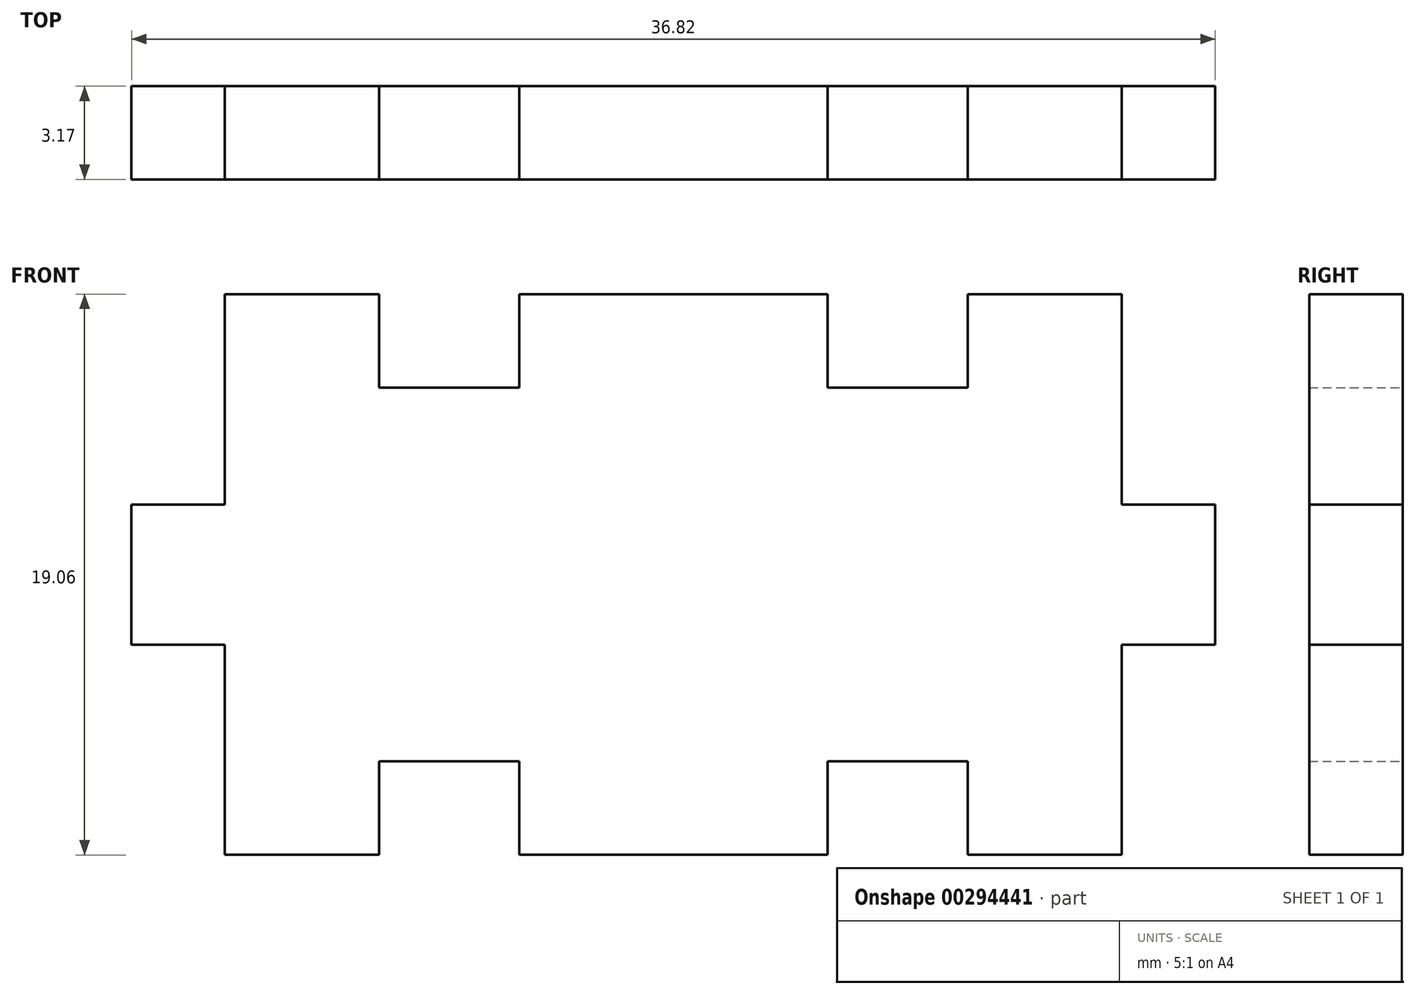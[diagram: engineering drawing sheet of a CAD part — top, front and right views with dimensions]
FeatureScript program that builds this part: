
annotation { "Feature Type Name" : "Feature", "Feature Type Description" : "" }
export const myFeature = defineFeature(function(context is Context, id is Id, definition is map)
    precondition{}
    {
        {
            var Q0;
            Q0=qCreatedBy(makeId("Front.planeOp"),FACE);
            var sketch = newSketch(context, id + "F0", { "sketchPlane" : qUnion([Q0])});
            skLineSegment(sketch, "E0.bottom", {"start": v(15.24, 9.52) * mm, "end": v(-15.24, 9.53) * mm});
            skLineSegment(sketch, "E0.top", {"start": v(15.24, -9.53) * mm, "end": v(-15.24, -9.52) * mm});
            skLineSegment(sketch, "E0.left", {"start": v(15.24, 9.53) * mm, "end": v(15.24, -9.53) * mm});
            skLineSegment(sketch, "E0.right", {"start": v(-15.24, 9.53) * mm, "end": v(-15.24, -9.53) * mm});
            skPoint(sketch, "E0.middle", {"position": v(0, 0) * mm});
            skLineSegment(sketch, "E1", {"start": v(0, 9.53) * mm, "end": v(0, -9.53) * mm});
            skLineSegment(sketch, "E2", {"start": v(-15.24, 0) * mm, "end": v(15.24, 0) * mm});
            skLineSegment(sketch, "E3", {"start": v(7.62, 9.53) * mm, "end": v(7.62, -9.53) * mm});
            skLineSegment(sketch, "E4", {"start": v(-7.62, 9.53) * mm, "end": v(-7.62, -9.53) * mm});
            skLineSegment(sketch, "E5.bottom", {"start": v(18.41, 2.38) * mm, "end": v(12.06, 2.38) * mm});
            skLineSegment(sketch, "E5.top", {"start": v(18.41, -2.38) * mm, "end": v(12.06, -2.38) * mm});
            skLineSegment(sketch, "E5.left", {"start": v(18.41, 2.38) * mm, "end": v(18.41, -2.38) * mm});
            skLineSegment(sketch, "E5.right", {"start": v(12.07, 2.38) * mm, "end": v(12.07, -2.38) * mm});
            skPoint(sketch, "E5.middle", {"position": v(15.24, 0) * mm});
            skLineSegment(sketch, "E6.bottom", {"start": v(-18.41, 2.38) * mm, "end": v(-12.07, 2.38) * mm});
            skLineSegment(sketch, "E6.top", {"start": v(-18.41, -2.38) * mm, "end": v(-12.07, -2.38) * mm});
            skLineSegment(sketch, "E6.left", {"start": v(-18.41, 2.38) * mm, "end": v(-18.41, -2.38) * mm});
            skLineSegment(sketch, "E6.right", {"start": v(-12.07, 2.38) * mm, "end": v(-12.07, -2.38) * mm});
            skPoint(sketch, "E6.middle", {"position": v(-15.24, 0) * mm});
            skLineSegment(sketch, "E7.bottom", {"start": v(10, 6.35) * mm, "end": v(5.24, 6.35) * mm});
            skLineSegment(sketch, "E7.top", {"start": v(10, 12.7) * mm, "end": v(5.24, 12.7) * mm});
            skLineSegment(sketch, "E7.left", {"start": v(10, 6.35) * mm, "end": v(10, 12.7) * mm});
            skLineSegment(sketch, "E7.right", {"start": v(5.24, 6.35) * mm, "end": v(5.24, 12.7) * mm});
            skPoint(sketch, "E7.middle", {"position": v(7.62, 9.53) * mm});
            skLineSegment(sketch, "E8.bottom", {"start": v(-5.24, 6.35) * mm, "end": v(-10, 6.35) * mm});
            skLineSegment(sketch, "E8.top", {"start": v(-5.24, 12.7) * mm, "end": v(-10, 12.7) * mm});
            skLineSegment(sketch, "E8.left", {"start": v(-5.24, 6.35) * mm, "end": v(-5.24, 12.7) * mm});
            skLineSegment(sketch, "E8.right", {"start": v(-10, 6.35) * mm, "end": v(-10, 12.7) * mm});
            skPoint(sketch, "E8.middle", {"position": v(-7.62, 9.53) * mm});
            skLineSegment(sketch, "E9.bottom", {"start": v(-5.24, -6.35) * mm, "end": v(-10, -6.35) * mm});
            skLineSegment(sketch, "E9.top", {"start": v(-5.24, -12.7) * mm, "end": v(-10, -12.7) * mm});
            skLineSegment(sketch, "E9.left", {"start": v(-5.24, -6.35) * mm, "end": v(-5.24, -12.7) * mm});
            skLineSegment(sketch, "E9.right", {"start": v(-10, -6.35) * mm, "end": v(-10, -12.7) * mm});
            skPoint(sketch, "E9.middle", {"position": v(-7.62, -9.53) * mm});
            skLineSegment(sketch, "E10.bottom", {"start": v(10, -6.35) * mm, "end": v(5.24, -6.35) * mm});
            skLineSegment(sketch, "E10.top", {"start": v(10, -12.7) * mm, "end": v(5.24, -12.7) * mm});
            skLineSegment(sketch, "E10.left", {"start": v(10, -6.35) * mm, "end": v(10, -12.7) * mm});
            skLineSegment(sketch, "E10.right", {"start": v(5.24, -6.35) * mm, "end": v(5.24, -12.7) * mm});
            skPoint(sketch, "E10.middle", {"position": v(7.62, -9.53) * mm});
            skSolve(sketch);
        }
        {
            var Q0;
            {var subQ0=sQuery(id+"F0.wireOp",EDGE,"E0.right");var subQ1=sQuery(id+"F0.wireOp",EDGE,"E0.bottom");var subQ2=makeQuery(id+"F0.imprint","INTERSECT",VERTEX,{"derivedFrom":[subQ1,subQ0]});Q0=makeQuery(id+"F0.imprint","IMPRINT",FACE,{"disambiguationData":[TD([[makeQuery(id+"F0.imprint","IMPRINT",EDGE,{"disambiguationData":[TD([[subQ2,1.0]])],"derivedFrom":subQ1}),1.0]])]});}
            var Q1;
            {var subQ5=sQuery(id+"F0.wireOp",EDGE,"E1");var subQ6=sQuery(id+"F0.wireOp",EDGE,"E0.bottom");var subQ7=makeQuery(id+"F0.imprint","INTERSECT",VERTEX,{"derivedFrom":[subQ6,subQ5]});Q1=makeQuery(id+"F0.imprint","IMPRINT",FACE,{"disambiguationData":[TD([[makeQuery(id+"F0.imprint","IMPRINT",EDGE,{"disambiguationData":[TD([[subQ7,-1.0]])],"derivedFrom":subQ6}),1.0]])]});}
            var Q2;
            {var subQ1=sQuery(id+"F0.wireOp",EDGE,"E1");var subQ5=sQuery(id+"F0.wireOp",EDGE,"E0.bottom");var subQ6=makeQuery(id+"F0.imprint","INTERSECT",VERTEX,{"derivedFrom":[subQ5,subQ1]});Q2=makeQuery(id+"F0.imprint","IMPRINT",FACE,{"disambiguationData":[TD([[makeQuery(id+"F0.imprint","IMPRINT",EDGE,{"disambiguationData":[TD([[subQ6,1.0]])],"derivedFrom":subQ5}),1.0]])]});}
            var Q3;
            {var subQ5=sQuery(id+"F0.wireOp",EDGE,"E0.left");var subQ6=sQuery(id+"F0.wireOp",EDGE,"E0.bottom");var subQ7=makeQuery(id+"F0.imprint","INTERSECT",VERTEX,{"derivedFrom":[subQ6,subQ5]});Q3=makeQuery(id+"F0.imprint","IMPRINT",FACE,{"disambiguationData":[TD([[makeQuery(id+"F0.imprint","IMPRINT",EDGE,{"disambiguationData":[TD([[subQ7,-1.0]])],"derivedFrom":subQ6}),1.0]])]});}
            var Q4;
            {var subQ0=sQuery(id+"F0.wireOp",EDGE,"E2");var subQ1=sQuery(id+"F0.wireOp",EDGE,"E0.left");var subQ2=makeQuery(id+"F0.imprint","INTERSECT",VERTEX,{"derivedFrom":[subQ1,subQ0]});Q4=makeQuery(id+"F0.imprint","IMPRINT",FACE,{"disambiguationData":[TD([[makeQuery(id+"F0.imprint","IMPRINT",EDGE,{"disambiguationData":[TD([[subQ2,1.0]])],"derivedFrom":subQ1}),-1.0]])]});}
            var Q5;
            {var subQ0=sQuery(id+"F0.wireOp",EDGE,"E2");var subQ1=sQuery(id+"F0.wireOp",EDGE,"E0.left");var subQ2=makeQuery(id+"F0.imprint","INTERSECT",VERTEX,{"derivedFrom":[subQ1,subQ0]});Q5=makeQuery(id+"F0.imprint","IMPRINT",FACE,{"disambiguationData":[TD([[makeQuery(id+"F0.imprint","IMPRINT",EDGE,{"disambiguationData":[TD([[subQ2,-1.0]])],"derivedFrom":subQ1}),-1.0]])]});}
            var Q6;
            {var subQ0=sQuery(id+"F0.wireOp",EDGE,"E5.left");Q6=makeQuery(id+"F0.imprint","IMPRINT",FACE,{"disambiguationData":[TD([[makeQuery(id+"F0.imprint","IMPRINT",EDGE,{"derivedFrom":subQ0}),-1.0]])]});}
            var Q7;
            {var subQ5=sQuery(id+"F0.wireOp",EDGE,"E0.left");var subQ6=sQuery(id+"F0.wireOp",EDGE,"E0.top");var subQ7=makeQuery(id+"F0.imprint","INTERSECT",VERTEX,{"derivedFrom":[subQ6,subQ5]});Q7=makeQuery(id+"F0.imprint","IMPRINT",FACE,{"disambiguationData":[TD([[makeQuery(id+"F0.imprint","IMPRINT",EDGE,{"disambiguationData":[TD([[subQ7,-1.0]])],"derivedFrom":subQ6}),-1.0]])]});}
            var Q8;
            {var subQ5=sQuery(id+"F0.wireOp",EDGE,"E1");var subQ7=sQuery(id+"F0.wireOp",EDGE,"E0.top");var subQ8=makeQuery(id+"F0.imprint","INTERSECT",VERTEX,{"derivedFrom":[subQ7,subQ5]});Q8=makeQuery(id+"F0.imprint","IMPRINT",FACE,{"disambiguationData":[TD([[makeQuery(id+"F0.imprint","IMPRINT",EDGE,{"disambiguationData":[TD([[subQ8,1.0]])],"derivedFrom":subQ7}),-1.0]])]});}
            var Q9;
            {var subQ7=sQuery(id+"F0.wireOp",EDGE,"E0.top");var subQ9=sQuery(id+"F0.wireOp",EDGE,"E1");var subQ11=makeQuery(id+"F0.imprint","INTERSECT",VERTEX,{"derivedFrom":[subQ7,subQ9]});Q9=makeQuery(id+"F0.imprint","IMPRINT",FACE,{"disambiguationData":[TD([[makeQuery(id+"F0.imprint","IMPRINT",EDGE,{"disambiguationData":[TD([[subQ11,-1.0]])],"derivedFrom":subQ7}),-1.0]])]});}
            var Q10;
            {var subQ7=sQuery(id+"F0.wireOp",EDGE,"E0.right");var subQ8=sQuery(id+"F0.wireOp",EDGE,"E0.top");var subQ9=makeQuery(id+"F0.imprint","INTERSECT",VERTEX,{"derivedFrom":[subQ8,subQ7]});Q10=makeQuery(id+"F0.imprint","IMPRINT",FACE,{"disambiguationData":[TD([[makeQuery(id+"F0.imprint","IMPRINT",EDGE,{"disambiguationData":[TD([[subQ9,1.0]])],"derivedFrom":subQ8}),-1.0]])]});}
            var Q11;
            {var subQ0=sQuery(id+"F0.wireOp",EDGE,"E2");var subQ1=sQuery(id+"F0.wireOp",EDGE,"E0.right");var subQ2=makeQuery(id+"F0.imprint","INTERSECT",VERTEX,{"derivedFrom":[subQ1,subQ0]});Q11=makeQuery(id+"F0.imprint","IMPRINT",FACE,{"disambiguationData":[TD([[makeQuery(id+"F0.imprint","IMPRINT",EDGE,{"disambiguationData":[TD([[subQ2,-1.0]])],"derivedFrom":subQ1}),1.0]])]});}
            var Q12;
            {var subQ0=sQuery(id+"F0.wireOp",EDGE,"E2");var subQ1=sQuery(id+"F0.wireOp",EDGE,"E0.right");var subQ2=makeQuery(id+"F0.imprint","INTERSECT",VERTEX,{"derivedFrom":[subQ1,subQ0]});Q12=makeQuery(id+"F0.imprint","IMPRINT",FACE,{"disambiguationData":[TD([[makeQuery(id+"F0.imprint","IMPRINT",EDGE,{"disambiguationData":[TD([[subQ2,1.0]])],"derivedFrom":subQ1}),1.0]])]});}
            var Q13;
            {var subQ0=sQuery(id+"F0.wireOp",EDGE,"E6.left");Q13=makeQuery(id+"F0.imprint","IMPRINT",FACE,{"disambiguationData":[TD([[makeQuery(id+"F0.imprint","IMPRINT",EDGE,{"derivedFrom":subQ0}),1.0]])]});}
            extrude(context, id + "F1", {"entities" : qUnion([Q0, Q1, Q2, Q3, Q4, Q5, Q6, Q7, Q8, Q9, Q10, Q11, Q12, Q13]), "depth" : 3.17 * mm});
        }
    });
